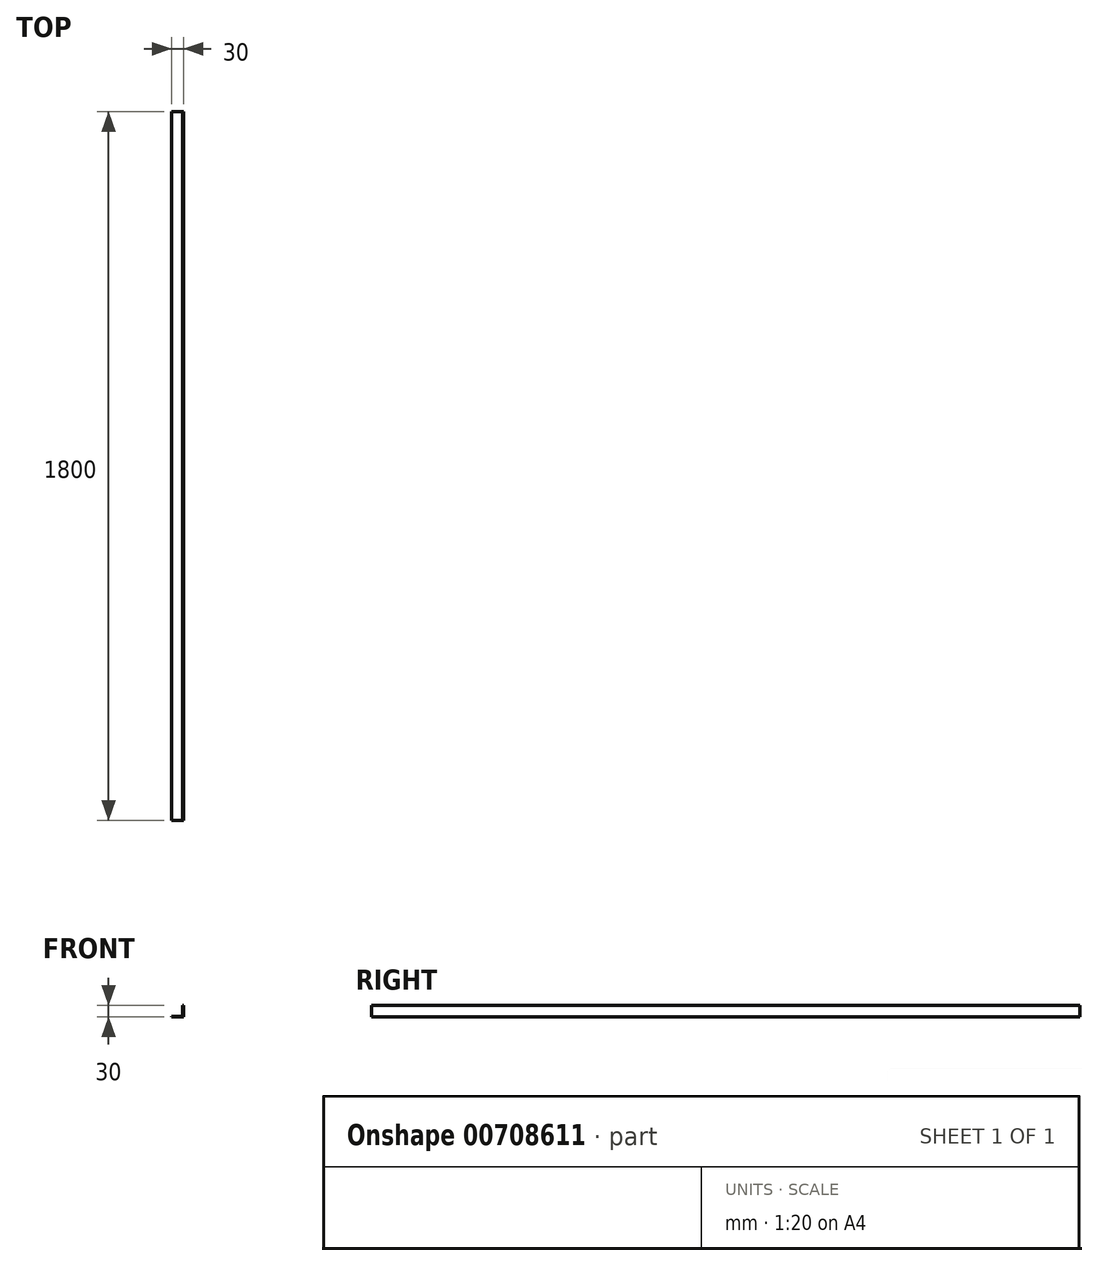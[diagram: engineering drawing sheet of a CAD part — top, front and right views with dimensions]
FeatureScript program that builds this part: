
annotation { "Feature Type Name" : "Feature", "Feature Type Description" : "" }
export const myFeature = defineFeature(function(context is Context, id is Id, definition is map)
    precondition{}
    {
        {
            var Q0;
            Q0=qCreatedBy(makeId("Front.planeOp"),FACE);
            var sketch = newSketch(context, id + "F0", { "sketchPlane" : qUnion([Q0])});
            skLineSegment(sketch, "E0", {"start": v(0, 0) * mm, "end": v(30, 0) * mm});
            skLineSegment(sketch, "E1", {"start": v(30, 0) * mm, "end": v(30, 30) * mm});
            skLineSegment(sketch, "E2", {"start": v(30, 30) * mm, "end": v(28, 30) * mm});
            skLineSegment(sketch, "E3", {"start": v(28, 30) * mm, "end": v(28, 2) * mm});
            skLineSegment(sketch, "E4", {"start": v(28, 2) * mm, "end": v(0, 2) * mm});
            skLineSegment(sketch, "E5", {"start": v(0, 2) * mm, "end": v(0, 0) * mm});
            skSolve(sketch);
        }
        {
            var Q0;
            Q0=makeQuery(id+"F0.imprint","IMPRINT",FACE,{"disambiguationData":[TD([[makeQuery(id+"F0.imprint","IMPRINT",EDGE,{"derivedFrom":sQuery(id+"F0.wireOp",EDGE,"E0")}),1.0]])]});
            extrude(context, id + "F1", {"entities" : qUnion([Q0]), "depth" : 1800 * mm, "offsetDistance" : 25 * mm});
        }
    });
